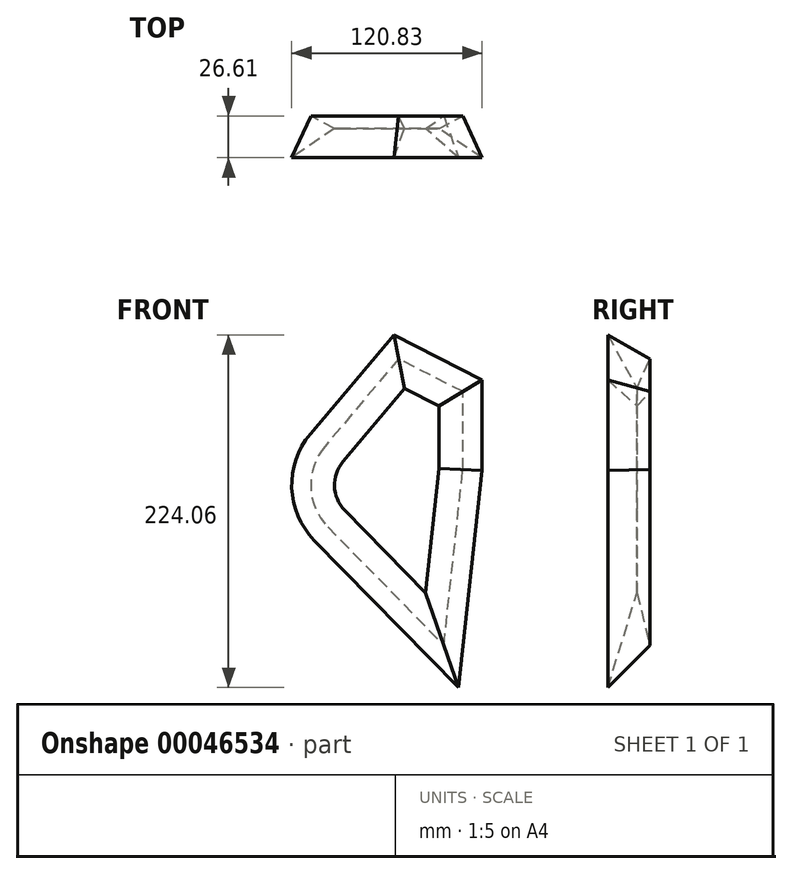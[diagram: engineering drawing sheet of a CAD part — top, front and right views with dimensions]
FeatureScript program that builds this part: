
annotation { "Feature Type Name" : "Feature", "Feature Type Description" : "" }
export const myFeature = defineFeature(function(context is Context, id is Id, definition is map)
    precondition{}
    {
        {
            var Q0;
            Q0=qCreatedBy(makeId("Top.planeOp"),FACE);
            var sketch = newSketch(context, id + "F0", { "sketchPlane" : qUnion([Q0])});
            skLineSegment(sketch, "E0", {"start": v(-1.93, 20.15) * mm, "end": v(-16.96, 12.05) * mm});
            skLineSegment(sketch, "E1", {"start": v(-16.96, 12.05) * mm, "end": v(10.22, -6.46) * mm});
            skLineSegment(sketch, "E2", {"start": v(-1.93, 20.15) * mm, "end": v(10.22, -6.46) * mm});
            skSolve(sketch);
        }
        {
            var Q0;
            Q0=qCreatedBy(makeId("Front.planeOp"),FACE);
            var sketch = newSketch(context, id + "F1", { "sketchPlane" : qUnion([Q0])});
            skLineSegment(sketch, "E3", {"start": v(0, 0) * mm, "end": v(0, 50.8) * mm});
            skLineSegment(sketch, "E4", {"start": v(0, 50.8) * mm, "end": v(-43.14, 72.92) * mm});
            skLineSegment(sketch, "E5", {"start": v(-43.14, 72.92) * mm, "end": v(-90.98, 16.15) * mm});
            skLineSegment(sketch, "E6", {"start": v(-88.97, -37.6) * mm, "end": v(-12.48, -115.73) * mm});
            skPoint(sketch, "E7.visualSharp", {"position": v(-114.4, -11.64) * mm});
            skArc(sketch, "E7.filletArc", {"start": v(-90.98, 16.15) * mm, "mid": v(-100.36, -11.11) * mm, "end": v(-88.97, -37.6) * mm});
            skLineSegment(sketch, "E8", {"start": v(-12.48, -115.73) * mm, "end": v(0, 0) * mm});
            skSolve(sketch);
        }
        {
            var Q0;
            Q0 = qSketchRegion(id + "F0", true);
            var Q1;
            Q1 = qConstructionFilter(qBodyType(qCreatedBy(id + "F1" ,EDGE), BodyType.WIRE), ConstructionObject.NO);
            sweep(context, id + "F2", {"profiles" : qUnion([Q0]), "path" : qUnion([Q1])});
        }
    });
